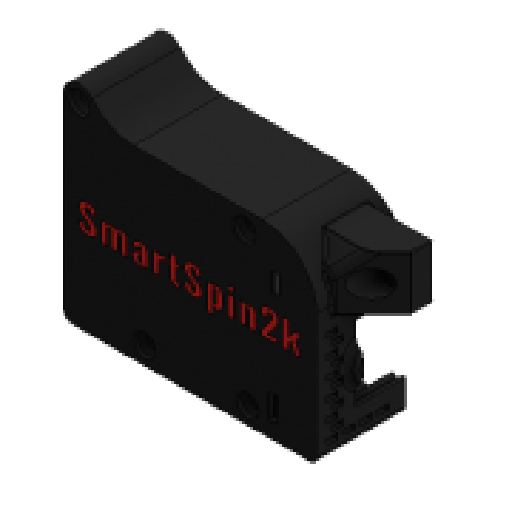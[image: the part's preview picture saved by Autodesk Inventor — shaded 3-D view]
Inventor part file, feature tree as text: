
AUTODESK INVENTOR PART (.ipt)
format: ipt  version: 2023 (Build 270158000, 158)  size: 1,613,312 bytes
history: native  units: mm
features: extrude x1, sketch x1, other x1, projected_geometry x1
ambient origin geometry x8: Origin, YZ Plane, XZ Plane, XY Plane, X Axis, Y Axis, Z Axis, Center Point
bodies: Solid1 (feature_tree), Solid2 (feature_tree)
feature tree (4):
  extrude  "Extrusion1"  [1 undecoded]
  sketch  "Sketch1"  dims[d0=10.0mm d1=0.0mm]
  other  "_Body_Drawing_-_Fillet22_"
  projected_geometry  "Project Cut Edges1"
note: 1 required parameter value undecoded (feature->parameter linkage not recoverable at this tier; creation-order binding heuristic only, values carry confidence <= 0.55)
